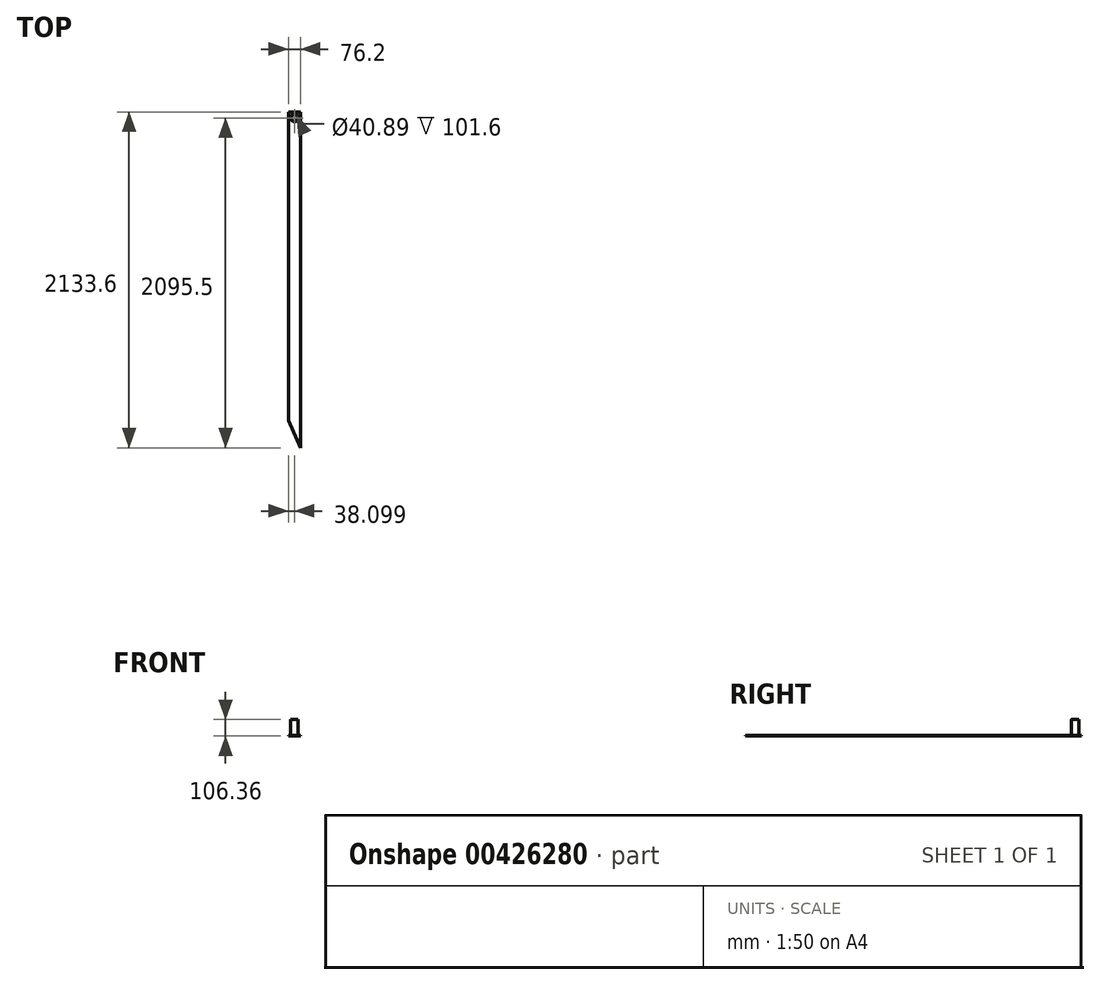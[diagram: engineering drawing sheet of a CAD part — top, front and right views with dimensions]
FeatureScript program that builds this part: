
annotation { "Feature Type Name" : "Feature", "Feature Type Description" : "" }
export const myFeature = defineFeature(function(context is Context, id is Id, definition is map)
    precondition{}
    {
        {
            var Q0;
            Q0=qCreatedBy(makeId("Top.planeOp"),FACE);
            var sketch = newSketch(context, id + "F0", { "sketchPlane" : qUnion([Q0])});
            skLineSegment(sketch, "E0.bottom", {"start": v(337.86, 853.8) * mm, "end": v(414.06, 853.8) * mm});
            skLineSegment(sketch, "E0.top", {"start": v(337.86, -1279.8) * mm, "end": v(414.06, -1279.8) * mm});
            skLineSegment(sketch, "E0.left", {"start": v(337.86, 853.8) * mm, "end": v(337.86, -1279.8) * mm});
            skLineSegment(sketch, "E0.right", {"start": v(414.06, 853.8) * mm, "end": v(414.06, -1279.8) * mm});
            skSolve(sketch);
        }
        {
            var Q0;
            Q0 = qSketchRegion(id + "F0", true);
            extrude(context, id + "F1", {"entities" : qUnion([Q0]), "oppositeDirection" : true, "depth" : 4.76 * mm});
        }
        {
            var Q0;
            Q0=makeQuery(id+"F1.opExtrude","CAP_FACE",FACE,{"disambiguationData":[OSD([sQuery(id+"F0.wireOp",EDGE,"E0.bottom"),sQuery(id+"F0.wireOp",EDGE,"E0.top"),sQuery(id+"F0.wireOp",EDGE,"E0.left"),sQuery(id+"F0.wireOp",EDGE,"E0.right")])],"isStart":true});
            var sketch = newSketch(context, id + "F2", { "sketchPlane" : qUnion([Q0])});
            skCircle(sketch, "E1", {"center": v(375.96, 815.7) * mm, "radius": 24.13 * mm});
            skCircle(sketch, "E2", {"center": v(375.96, 815.7) * mm, "radius": 20.45 * mm});
            skSolve(sketch);
        }
        {
            var Q0;
            Q0=makeQuery(id+"F2.imprint","IMPRINT",FACE,{"disambiguationData":[TD([[makeQuery(id+"F2.imprint","IMPRINT",EDGE,{"derivedFrom":sQuery(id+"F2.wireOp",EDGE,"E1")}),1.0]])]});
            var Q1;
            Q1=sQuery(id+"F2.wireOp",EDGE,"E1");
            var Q2;
            Q2=sQuery(id+"F2.wireOp",EDGE,"E2");
            extrude(context, id + "F3", {"entities" : qUnion([Q0]), "operationType" : NewBodyOperationType.ADD, "surfaceEntities" : qUnion([Q1, Q2]), "depth" : 101.6 * mm});
        }
        {
            var Q0;
            {var subQ0=sQuery(id+"F0.wireOp",EDGE,"E0.left");var subQ1=sQuery(id+"F0.wireOp",EDGE,"E0.top");var subQ2=sQuery(id+"F0.wireOp",EDGE,"E0.right");var subQ3=sQuery(id+"F0.wireOp",EDGE,"E0.bottom");Q0=makeQuery(id+"F3.boolean.opBoolean","SPLIT",FACE,{"disambiguationData":[TD([makeQuery(id+"F1.opExtrude","SWEPT_FACE",FACE,{"disambiguationData":[OSD([subQ3])]})])],"derivedFrom":makeQuery(id+"F1.opExtrude","CAP_FACE",FACE,{"disambiguationData":[OSD([subQ3,subQ1,subQ0,subQ2])],"isStart":false})});}
            var sketch = newSketch(context, id + "F4", { "sketchPlane" : qUnion([Q0])});
            skLineSegment(sketch, "E3", {"start": v(414.06, 1279.8) * mm, "end": v(337.86, 1107.85) * mm});
            skLineSegment(sketch, "E4", {"start": v(337.86, 1107.85) * mm, "end": v(337.86, 1279.8) * mm});
            skLineSegment(sketch, "E5", {"start": v(337.86, 1279.8) * mm, "end": v(414.06, 1279.8) * mm});
            skSolve(sketch);
        }
        {
            var Q0;
            Q0=makeQuery(id+"F4.imprint","IMPRINT",FACE,{"disambiguationData":[TD([[makeQuery(id+"F4.imprint","IMPRINT",EDGE,{"derivedFrom":sQuery(id+"F4.wireOp",EDGE,"E3")}),-1.0]])]});
            extrude(context, id + "F5", {"entities" : qUnion([Q0]), "operationType" : NewBodyOperationType.REMOVE, "oppositeDirection" : true, "depth" : 35.81 * mm});
        }
    });
